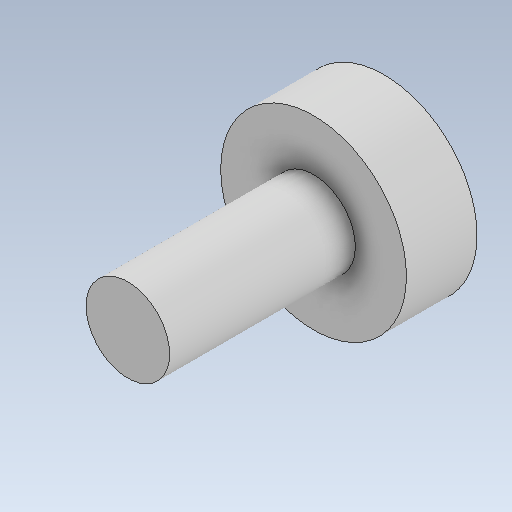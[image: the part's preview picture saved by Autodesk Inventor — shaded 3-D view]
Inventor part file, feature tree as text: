
AUTODESK INVENTOR PART (.ipt)
format: ipt  version: 2020 (Build 240168000, 168)  size: 108,544 bytes
history: native  units: mm
features: extrude x2, sketch x2
ambient origin geometry x8: Origin, YZ Plane, XZ Plane, XY Plane, X Axis, Y Axis, Z Axis, Center Point
bodies: Solid1 (feature_tree)
feature tree (4):
  extrude  "Extrusion1"  Depth=3.8mm TaperAngle=0.0deg
  extrude  "Extrusion2"  Depth=10.0mm TaperAngle=0.0deg
  sketch  "Sketch1"  dims[d0=10.0mm d1=3.8mm d2=0.0mm]
  sketch  "Sketch2"  dims[d3=4.5mm d4=10.0mm d5=0.0mm]
